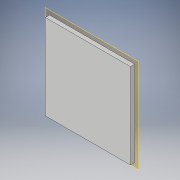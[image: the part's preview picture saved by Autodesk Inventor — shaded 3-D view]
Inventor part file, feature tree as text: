
AUTODESK INVENTOR PART (.ipt)
format: ipt  version: 2019.3 (Build 233278000, 278)  size: 90,624 bytes
history: native  units: in
note: dims shown in document units (in); Inventor stores cm internally (conversion verified against a paired STEP export)
features: sketch x2, other x1, extrude x1
ambient origin geometry x8: Origin, YZ Plane, XZ Plane, XY Plane, X Axis, Y Axis, Z Axis, Center Point
bodies: Body1 (feature_tree)
feature tree (4):
  other  "ソリッド1"
  sketch  "スケッチ1"
  extrude  "押し出し1"  Depth=0.7874in
  sketch  "スケッチ2"
